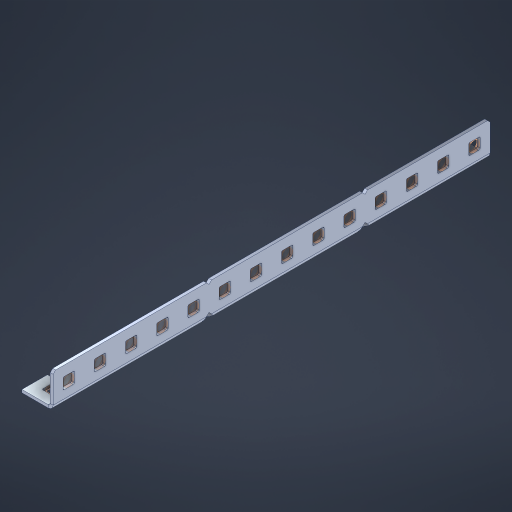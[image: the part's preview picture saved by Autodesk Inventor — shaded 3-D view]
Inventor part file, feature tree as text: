
AUTODESK INVENTOR PART (.ipt)
format: ipt  version: 2023 (Build 270158000, 158)  size: 773,120 bytes
history: native  units: in
note: dims shown in document units (in); Inventor stores cm internally (conversion verified against a paired STEP export)
features: other x49, extrude x40, sheet_metal_op x11, sketch x10, pattern_linear x2, mirror x1, chamfer x1
ambient origin geometry x8: Origin, YZ Plane, XZ Plane, XY Plane, X Axis, Y Axis, Z Axis, Center Point
bodies: Solid1 (feature_tree), Body (feature_tree)
feature tree (114):
  sheet_metal_op  "Flanges"
  other  "Flange Pattern Plane"
  other  "Flange Pattern Sketch"
  sheet_metal_op  "Flange Pattern"
  sheet_metal_op  "Body Pattern"
  pattern_linear  "Center Pattern"  Spacing1=0.0469in  [1 undecoded]
  other  "Arc Length"
  mirror  "Notch Mirror"
  pattern_linear  "Notch Pattern"  Spacing1=0.182in  [1 undecoded]
  chamfer  "End Chamfer"
  extrude  "Half Cut"  Depth=0.02in
  sketch  "Sketch1"  dims[d0=1.0in]
  other  "Plate1"
  sketch  "Sketch2"  dims[d1=7.0in]
  other  "Plate2"
  sheet_metal_op  "Bend1"
  sheet_metal_op  "Corner1"
  sketch  "Sketch3"  dims[d2=0.0469in]
  sketch  "Sketch7"  dims[d3=0.0469in]
  other  "Srf1"
  other  "Srf2"
  sketch  "Sketch8"  dims[d4=0.0234in]
  sketch  "Sketch9"  dims[d5=0.0938in]
  other  "Srf91"
  sheet_metal_op  "Body Pattern Sketch"
  other  "Srf92"
  sketch  "Sketch13"  dims[d6=0.0469in]
  sketch  "Sketch14"  dims[d7=0.5in d8=90.0deg d9=0.0312in]
  sketch  "Sketch15"  dims[d10=0.1875in]
  sketch  "Sketch16"  dims[d11=0.0469in d12=0.0469in d16=0.182in d17=0.02in d18=0.0469in d19=0.0in d20=0.25in d21=0.25in d38=5.5118in d40=0.5in d41=0.3937in d43=1.0in d46=0.172in d47=1.0in d48=0.0in d49=0.182in d50=0.02in d51=0.25in d52=0.25in d53=0.0469in d54=0.0in d55=0.172in d56=1.0in d57=0.0in d58=0.25in d60=5.5118in d62=0.5in d63=0.3937in d65=0.5in d85=0.1227in d86=0.1659in d88=0.04in d89=0.0469in d90=0.0in d91=0.04in d92=0.0491in d95=2.5in d96=0.04in d97=0.25in d98=45.0deg d99=0.25in d100=0.5in d101=0.0in d102=2.497in d106=0.182in d107=0.02in d108=0.5in d109=0.5in d110=0.0469in d111=0.0in d112=0.172in d113=0.5in d114=0.0in d117=0.5in d118=0.5in d119=0.5in]
  other  "Srf786"
  other  "Srf823"
  other  "Srf824"
  other  "Srf825"
  other  "Srf826"
  other  "Srf827"
  other  "Srf828"
  other  "Srf829"
  other  "Srf856"
  other  "Srf857"
  other  "Srf858"
  other  "Srf859"
  other  "Srf860"
  other  "Srf861"
  other  "Srf862"
  other  "Srf889"
  other  "Srf890"
  other  "Srf891"
  other  "Srf892"
  other  "Srf893"
  other  "Srf894"
  other  "Srf895"
  other  "Srf896"
  other  "Srf922"
  other  "Srf923"
  other  "Srf924"
  other  "Srf925"
  other  "Srf926"
  other  "Srf959"
  other  "Srf960"
  other  "Srf961"
  other  "Srf962"
  other  "Srf963"
  other  "Srf996"
  other  "Srf997"
  other  "Srf998"
  other  "Srf999"
  other  "Srf1000"
  sheet_metal_op  "Flange Stamp"
  sheet_metal_op  "Flange Circle"
  sheet_metal_op  "Body Stamp"
  sheet_metal_op  "Body Circle"
  other  "Center Stamp"
  other  "Center Circle"
  sheet_metal_op  "Notch"
  extrude  "ExtrusionSrf2"  Depth=0.0469in
  extrude  "ExtrusionSrf92"  TaperAngle=0.0deg  [1 undecoded]
  extrude  "ExtrusionSrf823"  Depth=0.25in
  extrude  "ExtrusionSrf824"  Depth=0.25in
  extrude  "ExtrusionSrf825"  Depth=0.5in
  extrude  "ExtrusionSrf826"  Depth=0.5in
  extrude  "ExtrusionSrf827"  Depth=1.0in TaperAngle=0.0deg
  extrude  "ExtrusionSrf828"  Depth=0.182in
  extrude  "ExtrusionSrf829"  Depth=0.02in
  extrude  "ExtrusionSrf856"  Depth=0.25in
  extrude  "ExtrusionSrf857"  Depth=0.25in
  extrude  "ExtrusionSrf858"  Depth=0.0469in
  extrude  "ExtrusionSrf859"  TaperAngle=0.0deg  [1 undecoded]
  extrude  "ExtrusionSrf860"  Depth=0.5in
  extrude  "ExtrusionSrf861"  Depth=1.0in TaperAngle=0.0deg
  extrude  "ExtrusionSrf862"  Depth=0.25in
  extrude  "ExtrusionSrf889"  Depth=0.5in
  extrude  "ExtrusionSrf890"  Depth=0.5in
  extrude  "ExtrusionSrf891"  Depth=0.5in
  extrude  "ExtrusionSrf892"  Depth=0.5in
  extrude  "ExtrusionSrf893"  Depth=0.5in
  extrude  "ExtrusionSrf894"  Depth=0.0469in
  extrude  "ExtrusionSrf895"  TaperAngle=0.0deg  [1 undecoded]
  extrude  "ExtrusionSrf896"  Depth=0.5in
  extrude  "ExtrusionSrf922"  Depth=0.5in
  extrude  "ExtrusionSrf923"  Depth=2.5in
  extrude  "ExtrusionSrf924"  Depth=0.25in TaperAngle=45.0deg
  extrude  "ExtrusionSrf925"  Depth=0.25in
  extrude  "ExtrusionSrf926"  Depth=0.5in TaperAngle=0.0deg
  extrude  "ExtrusionSrf959"  Depth=0.5in
  extrude  "ExtrusionSrf960"  Depth=0.182in
  extrude  "ExtrusionSrf961"  Depth=0.02in
  extrude  "ExtrusionSrf962"  Depth=0.5in
  extrude  "ExtrusionSrf963"  Depth=0.5in
  extrude  "ExtrusionSrf996"  Depth=0.0469in
  extrude  "ExtrusionSrf997"  TaperAngle=0.0deg  [1 undecoded]
  extrude  "ExtrusionSrf998"  Depth=0.5in
  extrude  "ExtrusionSrf999"  Depth=0.5in TaperAngle=0.0deg
  extrude  "ExtrusionSrf1000"  Depth=0.5in
note: 6 required parameter values undecoded (feature->parameter linkage not recoverable at this tier; creation-order binding heuristic only, values carry confidence <= 0.55)
